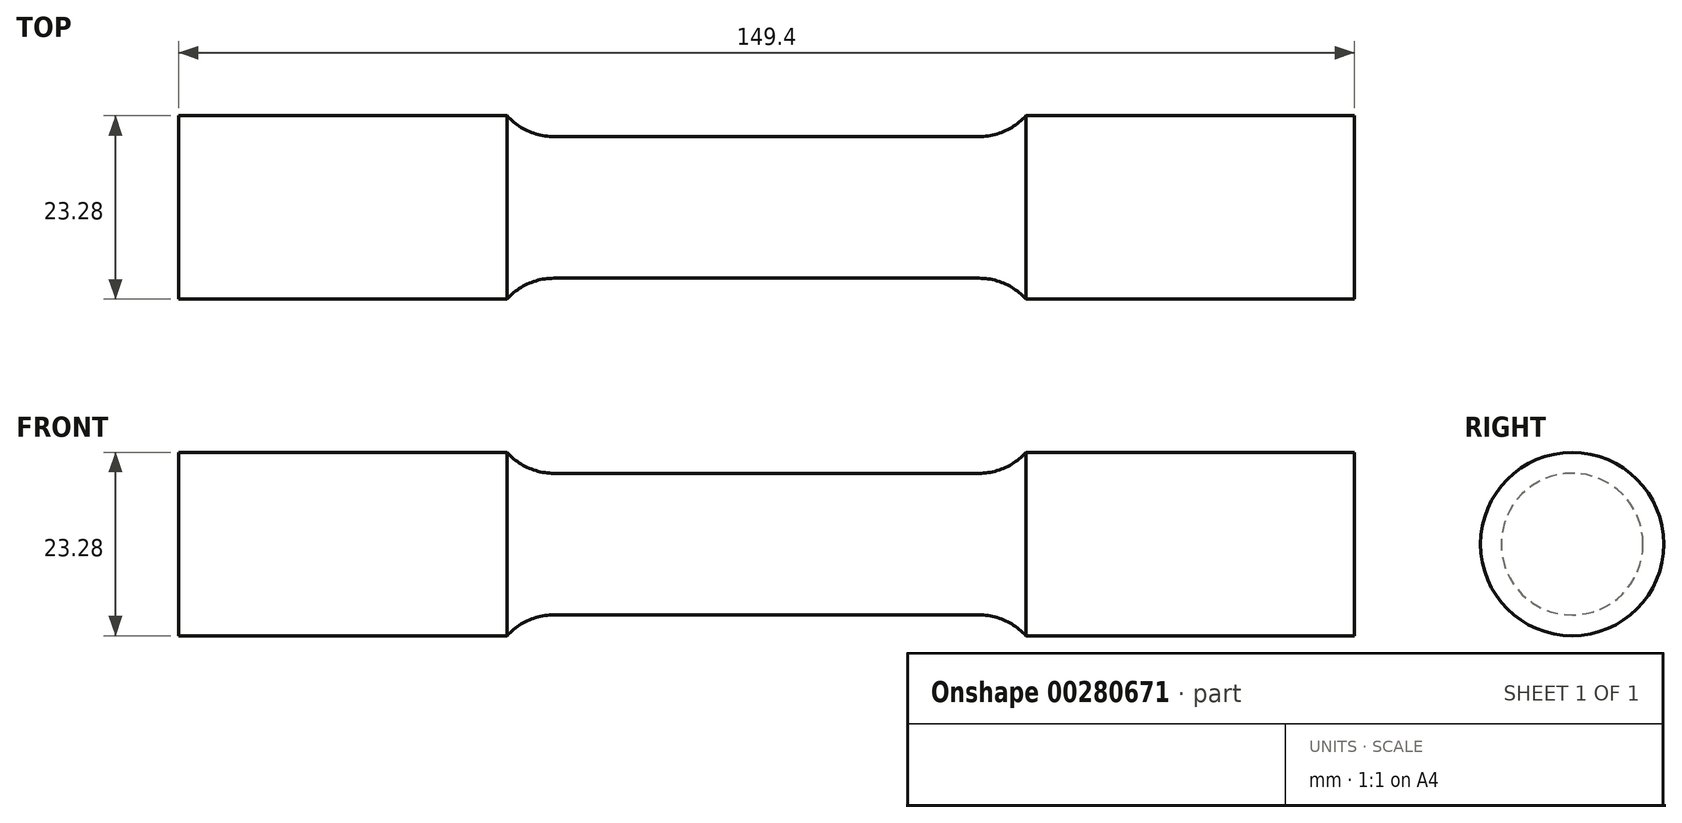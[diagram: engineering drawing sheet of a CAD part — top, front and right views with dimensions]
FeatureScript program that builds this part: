
annotation { "Feature Type Name" : "Feature", "Feature Type Description" : "" }
export const myFeature = defineFeature(function(context is Context, id is Id, definition is map)
    precondition{}
    {
        {
            var Q0;
            Q0=qCreatedBy(makeId("Front.planeOp"),FACE);
            var sketch = newSketch(context, id + "F0", { "sketchPlane" : qUnion([Q0])});
            skLineSegment(sketch, "E0", {"start": v(0, 9) * mm, "end": v(27, 9) * mm});
            skArc(sketch, "E1", {"start": v(27, 9) * mm, "mid": v(30.25, 9.69) * mm, "end": v(32.94, 11.64) * mm});
            skLineSegment(sketch, "E2", {"start": v(32.94, 11.64) * mm, "end": v(74.7, 11.64) * mm});
            skLineSegment(sketch, "E3", {"start": v(74.7, 11.64) * mm, "end": v(74.7, 0) * mm});
            skLineSegment(sketch, "E4.MirrorCS", {"start": v(0, 9) * mm, "end": v(-27, 9) * mm});
            skLineSegment(sketch, "E5.MirrorCS", {"start": v(-32.94, 11.64) * mm, "end": v(-74.7, 11.64) * mm});
            skArc(sketch, "E6.MirrorCS", {"start": v(-27, 9) * mm, "mid": v(-30.25, 9.69) * mm, "end": v(-32.94, 11.64) * mm});
            skLineSegment(sketch, "E7.MirrorCS", {"start": v(-74.7, 11.64) * mm, "end": v(-74.7, 0) * mm});
            skLineSegment(sketch, "E8", {"start": v(-74.7, 0) * mm, "end": v(74.7, 0) * mm});
            skSolve(sketch);
        }
        {
            var Q0;
            Q0 = qSketchRegion(id + "F0", true);
            var Q1;
            Q1=sQuery(id+"F0.wireOp",EDGE,"E8");
            revolve(context, id + "F1", {"entities" : qUnion([Q0]), "axis" : qUnion([Q1]), "revolveType" : RevolveType.FULL});
        }
    });
